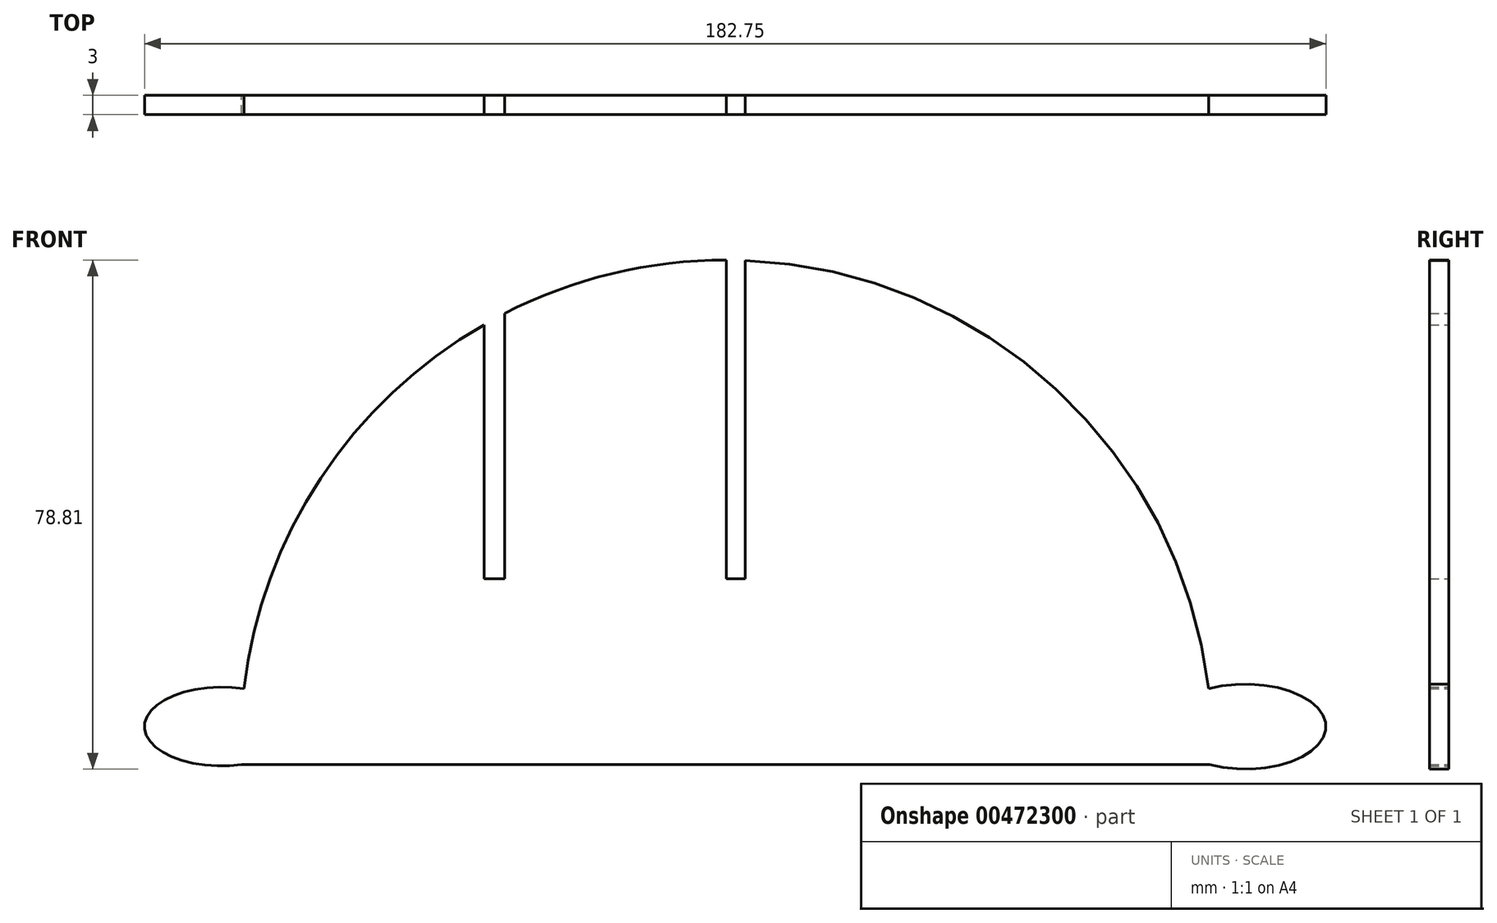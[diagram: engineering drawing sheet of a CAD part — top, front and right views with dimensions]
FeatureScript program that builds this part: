
annotation { "Feature Type Name" : "Feature", "Feature Type Description" : "" }
export const myFeature = defineFeature(function(context is Context, id is Id, definition is map)
    precondition{}
    {
        {
            var Q0;
            Q0=qCreatedBy(makeId("Front.planeOp"),FACE);
            var sketch = newSketch(context, id + "F0", { "sketchPlane" : qUnion([Q0])});
            skLineSegment(sketch, "E0", {"start": v(69.3, 0) * mm, "end": v(-80.7, 0) * mm});
            skArc(sketch, "E1.trimOffspring", {"start": v(68.84, 10.68) * mm, "mid": v(68.79, 11.2) * mm, "end": v(68.73, 11.71) * mm});
            skLineSegment(sketch, "E2", {"start": v(34.97, 28.75) * mm, "end": v(31.77, 28.75) * mm});
            skPoint(sketch, "E3.end.orphan", {"position": v(41.88, 28.75) * mm});
            skPoint(sketch, "E4.start.orphan", {"position": v(31.77, 67.94) * mm});
            skLineSegment(sketch, "E5", {"start": v(-2.8, 28.75) * mm, "end": v(-5.73, 28.75) * mm});
            skLineSegment(sketch, "E6", {"start": v(-40.03, 28.75) * mm, "end": v(-43.23, 28.75) * mm});
            skPoint(sketch, "E7.orphan", {"position": v(64.68, 28.75) * mm});
            skEllipticalArc(sketch, "E8", {});
            skPoint(sketch, "E9.orphan", {"position": v(-80.82, 0) * mm});
            skEllipticalArc(sketch, "E10", {});
            skArc(sketch, "E11.trimOffspring", {"start": v(68.85, 11.74) * mm, "mid": v(58, 42.73) * mm, "end": v(34.97, 66.13) * mm});
            skLineSegment(sketch, "E12", {"start": v(-40.03, 28.75) * mm, "end": v(-40.03, 69.85) * mm});
            skLineSegment(sketch, "E13", {"start": v(-43.23, 28.75) * mm, "end": v(-43.23, 68.11) * mm});
            skArc(sketch, "E14.trimOffspring", {"start": v(-43.23, 68.11) * mm, "mid": v(-68.8, 43.86) * mm, "end": v(-80.5, 10.62) * mm});
            skLineSegment(sketch, "E15", {"start": v(-2.8, 28.75) * mm, "end": v(-2.8, 78.07) * mm});
            skLineSegment(sketch, "E16", {"start": v(-5.73, 28.75) * mm, "end": v(-5.73, 78.13) * mm});
            skArc(sketch, "E17.trimOffspring", {"start": v(-5.73, 78.13) * mm, "mid": v(-23.38, 76.03) * mm, "end": v(-40.03, 69.85) * mm});
            skLineSegment(sketch, "E18", {"start": v(34.97, 28.75) * mm, "end": v(34.97, 66.13) * mm});
            skArc(sketch, "E19", {"start": v(69.3, 0) * mm, "mid": v(60.9, 37.62) * mm, "end": v(34.97, 66.13) * mm});
            skLineSegment(sketch, "E20", {"start": v(31.77, 67.94) * mm, "end": v(31.77, 28.75) * mm});
            skArc(sketch, "E21", {"start": v(69.3, 0) * mm, "mid": v(49.42, 53.97) * mm, "end": v(-2.8, 78.07) * mm});
            const initialGuessF0  = {"E8": [0.0745469480752945, 0.005894604604691267, 1, 0, 0.012467116117477417, 0.006575280191314619, 4.253351988137473, 2.056206815545136], "E10": [-0.08384214341640472, 0.005894604604691267, 1, 0, 0.011900432407855988, 0.006111084969047646, 1.2750591683167358, 4.979354728818344]};
            skSetInitialGuess(sketch, initialGuessF0);
            skSolve(sketch);
        }
        {
            var Q0;
            Q0 = qSketchRegion(id + "F0", true);
            extrude(context, id + "F1", {"entities" : qUnion([Q0]), "depth" : 3 * mm, "offsetDistance" : 25 * mm});
        }
    });
